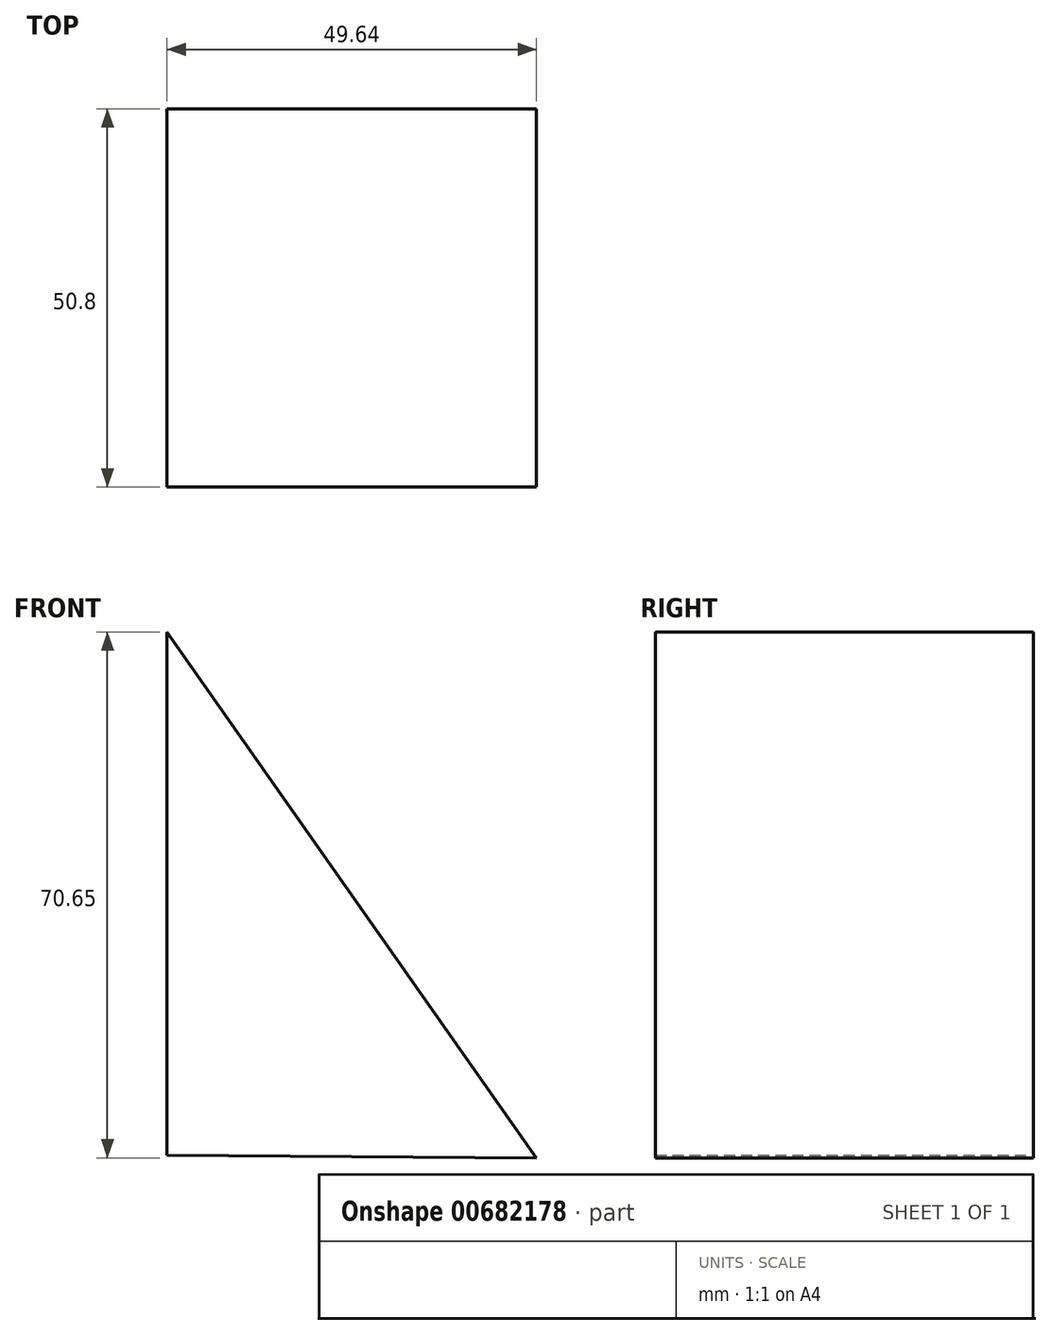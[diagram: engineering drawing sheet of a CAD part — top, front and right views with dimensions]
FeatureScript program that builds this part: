
annotation { "Feature Type Name" : "Feature", "Feature Type Description" : "" }
export const myFeature = defineFeature(function(context is Context, id is Id, definition is map)
    precondition{}
    {
        {
            var Q0;
            Q0=qCreatedBy(makeId("Front.planeOp"),FACE);
            var sketch = newSketch(context, id + "F0", { "sketchPlane" : qUnion([Q0])});
            skLineSegment(sketch, "E0", {"start": v(-53.94, 37.33) * mm, "end": v(-53.94, -32.94) * mm});
            skLineSegment(sketch, "E1", {"start": v(-53.94, 37.33) * mm, "end": v(-4.3, -33.32) * mm});
            skLineSegment(sketch, "E2", {"start": v(-53.94, -32.94) * mm, "end": v(-4.3, -33.32) * mm});
            skSolve(sketch);
        }
        {
            var Q0;
            Q0 = qSketchRegion(id + "F0", true);
            extrude(context, id + "F1", {"entities" : qUnion([Q0]), "depth" : 50.8 * mm, "offsetDistance" : 25.4 * mm});
        }
    });
